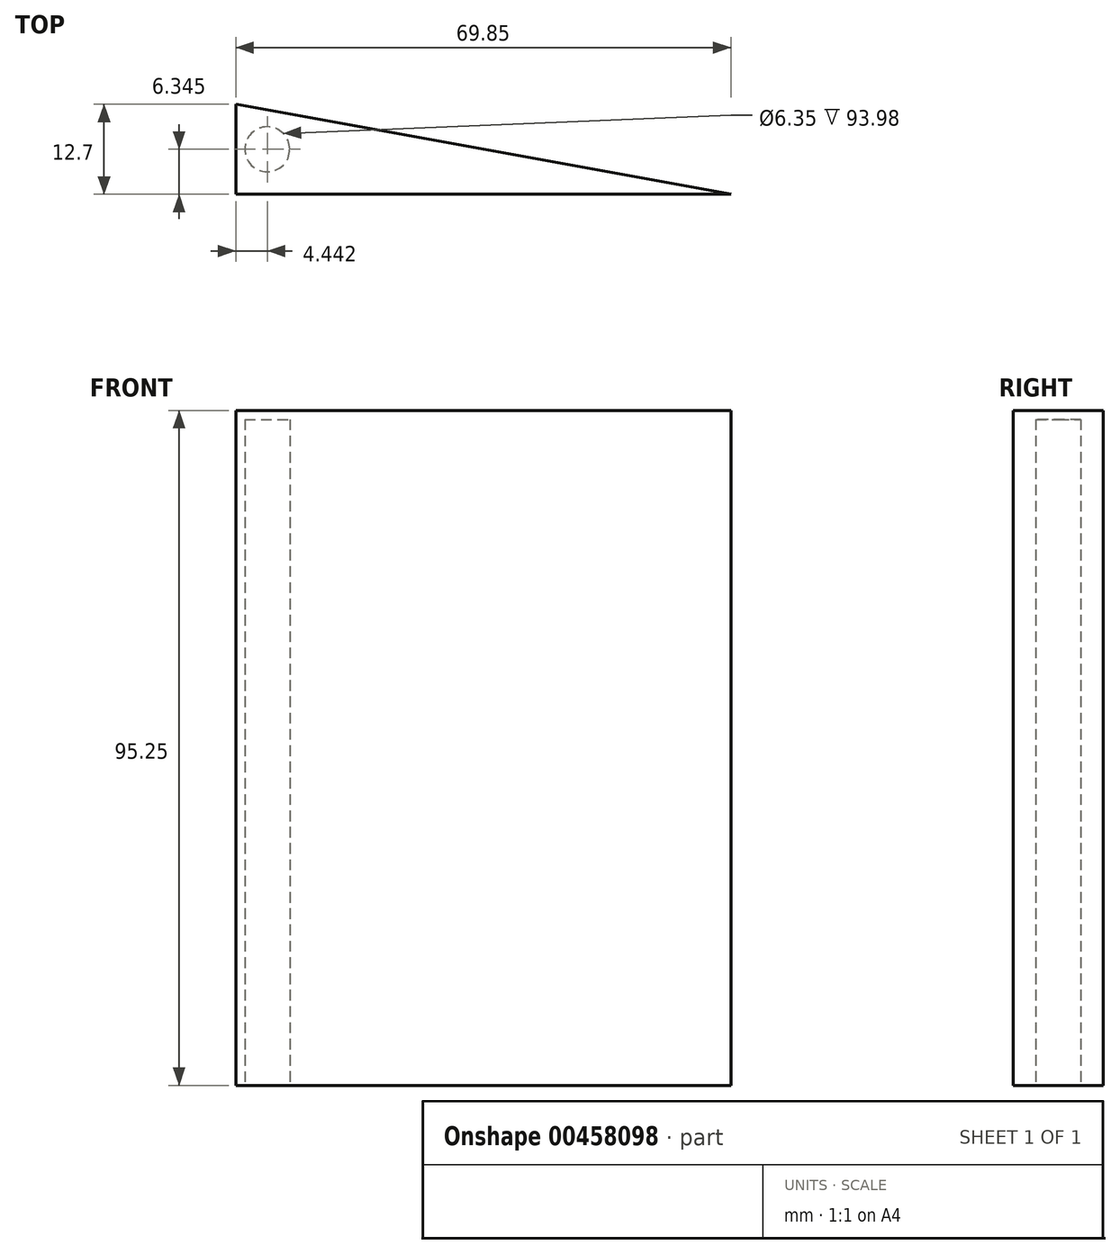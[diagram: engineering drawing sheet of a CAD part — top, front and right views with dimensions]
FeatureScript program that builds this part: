
annotation { "Feature Type Name" : "Feature", "Feature Type Description" : "" }
export const myFeature = defineFeature(function(context is Context, id is Id, definition is map)
    precondition{}
    {
        {
            var Q0;
            Q0=qCreatedBy(makeId("Top.planeOp"),FACE);
            var sketch = newSketch(context, id + "F0", { "sketchPlane" : qUnion([Q0])});
            skLineSegment(sketch, "E0", {"start": v(-52.41, 25.54) * mm, "end": v(17.44, 25.54) * mm});
            skLineSegment(sketch, "E1", {"start": v(-52.41, 25.54) * mm, "end": v(-52.41, 38.24) * mm});
            skLineSegment(sketch, "E2", {"start": v(-52.41, 38.24) * mm, "end": v(17.44, 25.54) * mm});
            skSolve(sketch);
        }
        {
            var Q0;
            Q0=makeQuery(id+"F0.imprint","IMPRINT",FACE,{"disambiguationData":[TD([[makeQuery(id+"F0.imprint","IMPRINT",EDGE,{"derivedFrom":sQuery(id+"F0.wireOp",EDGE,"E0")}),1.0]])]});
            extrude(context, id + "F1", {"entities" : qUnion([Q0]), "depth" : 95.25 * mm});
        }
        {
            var Q0;
            Q0=makeQuery(id+"F1.opExtrude","CAP_FACE",FACE,{"disambiguationData":[OSD([sQuery(id+"F0.wireOp",EDGE,"E0"),sQuery(id+"F0.wireOp",EDGE,"E1"),sQuery(id+"F0.wireOp",EDGE,"E2")])],"isStart":true});
            var sketch = newSketch(context, id + "F2", { "sketchPlane" : qUnion([Q0])});
            skLineSegment(sketch, "E3", {"start": v(-52.41, -31.89) * mm, "end": v(-51.14, -31.89) * mm});
            skLineSegment(sketch, "E4", {"start": v(-51.14, -31.89) * mm, "end": v(-47.97, -31.89) * mm});
            skCircle(sketch, "E5", {"center": v(-47.97, -31.89) * mm, "radius": 3.17 * mm});
            skSolve(sketch);
        }
        {
            var Q0;
            Q0=makeQuery(id+"F2.imprint","IMPRINT",FACE,{"disambiguationData":[TD([[makeQuery(id+"F2.imprint","IMPRINT",EDGE,{"derivedFrom":sQuery(id+"F2.wireOp",EDGE,"E5")}),1.0]])]});
            extrude(context, id + "F3", {"entities" : qUnion([Q0]), "operationType" : NewBodyOperationType.REMOVE, "oppositeDirection" : true, "depth" : 93.98 * mm});
        }
    });
